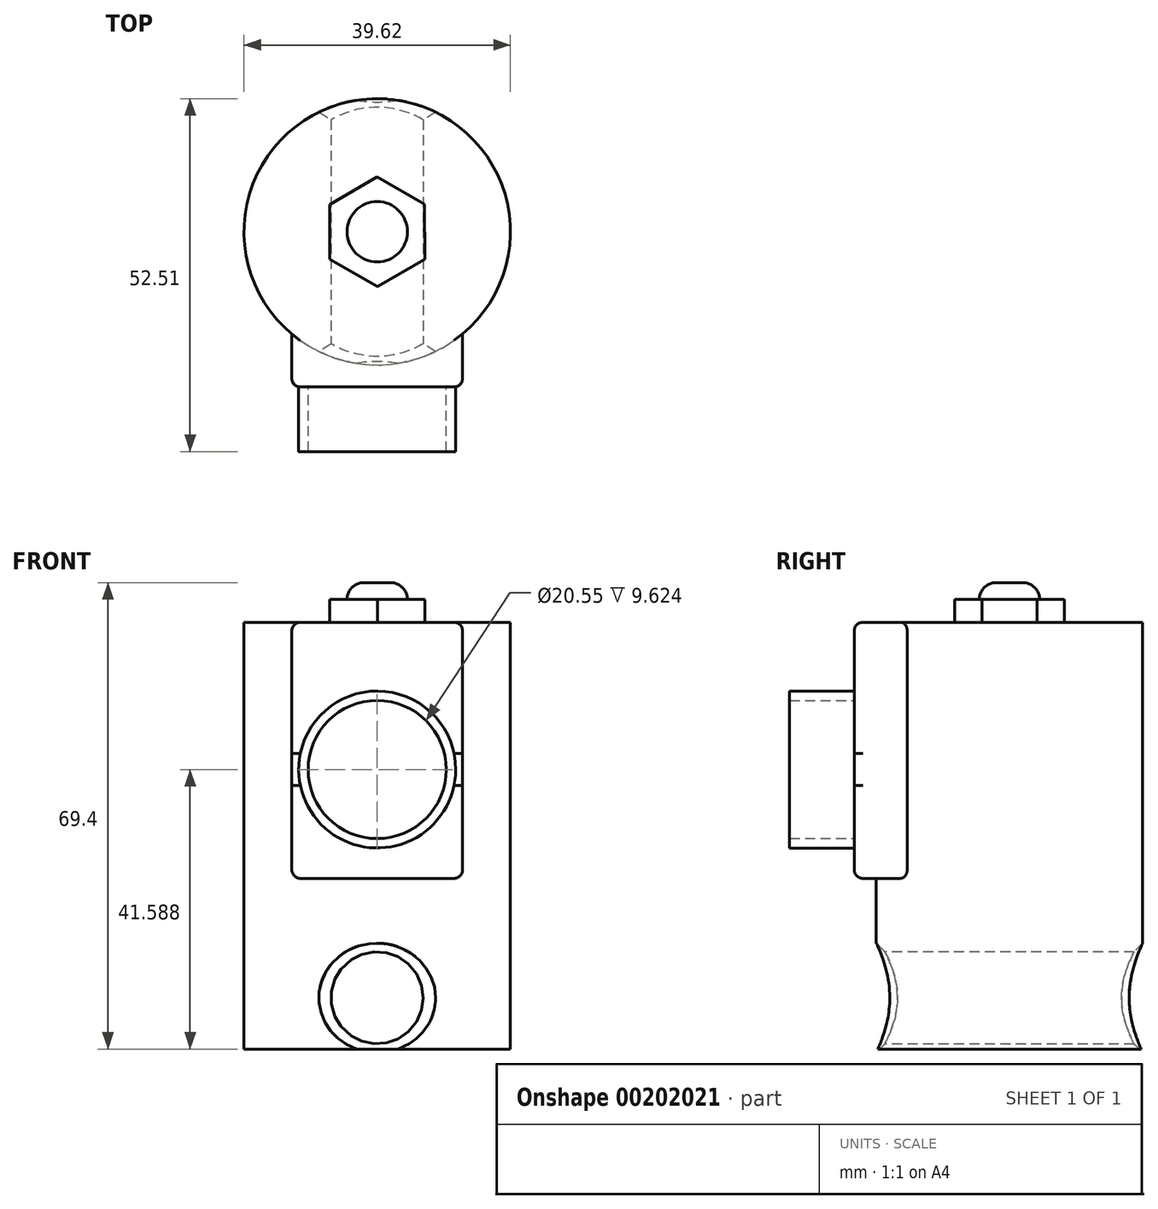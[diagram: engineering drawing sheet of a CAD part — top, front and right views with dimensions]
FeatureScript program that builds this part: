
annotation { "Feature Type Name" : "Feature", "Feature Type Description" : "" }
export const myFeature = defineFeature(function(context is Context, id is Id, definition is map)
    precondition{}
    {
        {
            var Q0;
            Q0=qCreatedBy(makeId("Top.planeOp"),FACE);
            var sketch = newSketch(context, id + "F0", { "sketchPlane" : qUnion([Q0])});
            skCircle(sketch, "E0", {"center": v(0, 0) * mm, "radius": 19.81 * mm});
            skLineSegment(sketch, "E1", {"start": v(0, 0) * mm, "end": v(0, -19.81) * mm});
            skSolve(sketch);
        }
        {
            var Q0;
            Q0=qSketchRegion(id+"F0",true);
            extrude(context, id + "F1", {"entities" : qUnion([Q0]), "depth" : 63.5 * mm});
        }
        {
            var Q0;
            Q0=qCreatedBy(makeId("Right.planeOp"),FACE);
            var sketch = newSketch(context, id + "F2", { "sketchPlane" : qUnion([Q0])});
            skLineSegment(sketch, "E2", {"start": v(-19.81, 0) * mm, "end": v(-19.81, 70.78) * mm});
            skSolve(sketch);
        }
        {
            var Q0;
            Q0=sQuery(id+"F2.wireOp",EDGE,"E2");
            cPlane(context, id + "F3", {"entities" : qUnion([Q0]), "cplaneType" : CPlaneType.LINE_ANGLE, "offset" : 25.4 * mm, "angle" : 90 * degree, "width" : 152.4 * mm, "height" : 152.4 * mm});
        }
        {
            var Q0;
            Q0=qCreatedBy(id+"F3.planeOp",FACE);
            var sketch = newSketch(context, id + "F4", { "sketchPlane" : qUnion([Q0])});
            skLineSegment(sketch, "E3", {"start": v(0, 0) * mm, "end": v(0, 7.62) * mm});
            skCircle(sketch, "E4", {"center": v(0, 7.62) * mm, "radius": 6.86 * mm});
            skSolve(sketch);
        }
        {
            var Q0;
            Q0=makeQuery(id+"F4.imprint","IMPRINT",FACE,{"disambiguationData":[TD([[makeQuery(id+"F4.imprint","IMPRINT",EDGE,{"derivedFrom":sQuery(id+"F4.wireOp",EDGE,"E4")}),1.0]])]});
            extrude(context, id + "F5", {"entities" : qUnion([Q0]), "operationType" : NewBodyOperationType.REMOVE, "depth" : 50.8 * mm});
        }
        {
            var Q0;
            Q0=qCreatedBy(id+"F3.planeOp",FACE);
            var sketch = newSketch(context, id + "F6", { "sketchPlane" : qUnion([Q0])});
            skLineSegment(sketch, "E5", {"start": v(0, 63.5) * mm, "end": v(0, 44.45) * mm});
            skLineSegment(sketch, "E6.bottom", {"start": v(-12.7, 63.5) * mm, "end": v(12.7, 63.5) * mm});
            skLineSegment(sketch, "E6.top", {"start": v(-12.7, 25.4) * mm, "end": v(12.7, 25.4) * mm});
            skLineSegment(sketch, "E6.left", {"start": v(-12.7, 63.5) * mm, "end": v(-12.7, 25.4) * mm});
            skLineSegment(sketch, "E6.right", {"start": v(12.7, 63.5) * mm, "end": v(12.7, 25.4) * mm});
            skPoint(sketch, "E6.middle", {"position": v(0, 44.45) * mm});
            skSolve(sketch);
        }
        {
            var Q0;
            Q0=makeQuery(id+"F6.imprint","IMPRINT",FACE,{"disambiguationData":[TD([[makeQuery(id+"F6.imprint","IMPRINT",EDGE,{"derivedFrom":sQuery(id+"F6.wireOp",EDGE,"E6.top")}),1.0]])]});
            extrude(context, id + "F7", {"entities" : qUnion([Q0]), "operationType" : NewBodyOperationType.ADD, "depth" : 25.4 * mm, "hasSecondDirection" : true, "secondDirectionOppositeDirection" : true, "secondDirectionDepth" : 3.27 * mm});
        }
        {
            var Q0;
            Q0=makeQuery(id+"F7.opExtrude","CAP_FACE",FACE,{"disambiguationData":[OSD([sQuery(id+"F6.wireOp",EDGE,"E6.bottom"),sQuery(id+"F6.wireOp",EDGE,"E6.top"),sQuery(id+"F6.wireOp",EDGE,"E6.left"),sQuery(id+"F6.wireOp",EDGE,"E6.right")])],"isStart":true});
            var sketch = newSketch(context, id + "F8", { "sketchPlane" : qUnion([Q0])});
            skCircle(sketch, "E7", {"center": v(0, 41.59) * mm, "radius": 11.67 * mm});
            skCircle(sketch, "E8", {"center": v(0, 41.59) * mm, "radius": 10.27 * mm});
            skSolve(sketch);
        }
        {
            var Q0;
            Q0=makeQuery(id+"F8.imprint","IMPRINT",FACE,{"disambiguationData":[TD([[makeQuery(id+"F8.imprint","IMPRINT",EDGE,{"derivedFrom":sQuery(id+"F8.wireOp",EDGE,"E7")}),1.0]])]});
            extrude(context, id + "F9", {"entities" : qUnion([Q0]), "operationType" : NewBodyOperationType.ADD, "depth" : 9.62 * mm});
        }
        {
            var Q0;
            Q0=makeQuery(id+"F7.boolean.opBoolean","MERGE",FACE,{"derivedFrom":[makeQuery(id+"F1.opExtrude","CAP_FACE",FACE,{"disambiguationData":[OSD([sQuery(id+"F0.wireOp",EDGE,"E0")])],"isStart":false}),makeQuery(id+"F7.opExtrude","SWEPT_FACE",FACE,{"disambiguationData":[OSD([sQuery(id+"F6.wireOp",EDGE,"E6.bottom")])]})]});
            var sketch = newSketch(context, id + "F10", { "sketchPlane" : qUnion([Q0])});
            skCircle(sketch, "E9.cCircle", {"center": v(0, 0) * mm, "radius": 8.16 * mm, "construction": true});
            skLineSegment(sketch, "E9.0", {"start": v(7.05, 4.1) * mm, "end": v(7.09, -4.06) * mm});
            skLineSegment(sketch, "E9.1", {"start": v(7.09, -4.06) * mm, "end": v(0.03, -8.16) * mm});
            skLineSegment(sketch, "E9.2", {"start": v(0.03, -8.16) * mm, "end": v(-7.05, -4.1) * mm});
            skLineSegment(sketch, "E9.3", {"start": v(-7.05, -4.1) * mm, "end": v(-7.09, 4.06) * mm});
            skLineSegment(sketch, "E9.4", {"start": v(-7.09, 4.06) * mm, "end": v(-0.03, 8.16) * mm});
            skLineSegment(sketch, "E9.5", {"start": v(-0.03, 8.16) * mm, "end": v(7.05, 4.1) * mm});
            skSolve(sketch);
        }
        {
            var Q0;
            Q0=makeQuery(id+"F10.imprint","IMPRINT",FACE,{"disambiguationData":[TD([[makeQuery(id+"F10.imprint","IMPRINT",EDGE,{"derivedFrom":sQuery(id+"F10.wireOp",EDGE,"E9.0")}),-1.0]])]});
            extrude(context, id + "F11", {"entities" : qUnion([Q0]), "operationType" : NewBodyOperationType.ADD, "depth" : 3.38 * mm});
        }
        {
            var Q0;
            Q0=makeQuery(id+"F11.opExtrude","CAP_FACE",FACE,{"disambiguationData":[OSD([sQuery(id+"F10.wireOp",EDGE,"E9.0"),sQuery(id+"F10.wireOp",EDGE,"E9.1"),sQuery(id+"F10.wireOp",EDGE,"E9.2"),sQuery(id+"F10.wireOp",EDGE,"E9.3"),sQuery(id+"F10.wireOp",EDGE,"E9.4"),sQuery(id+"F10.wireOp",EDGE,"E9.5")])],"isStart":false});
            var sketch = newSketch(context, id + "F12", { "sketchPlane" : qUnion([Q0])});
            skCircle(sketch, "E10", {"center": v(0, 0) * mm, "radius": 4.5 * mm});
            skSolve(sketch);
        }
        {
            var Q0;
            Q0=makeQuery(id+"F12.imprint","IMPRINT",FACE,{"disambiguationData":[TD([[makeQuery(id+"F12.imprint","IMPRINT",EDGE,{"derivedFrom":sQuery(id+"F12.wireOp",EDGE,"E10")}),1.0]])]});
            extrude(context, id + "F13", {"entities" : qUnion([Q0]), "operationType" : NewBodyOperationType.ADD, "depth" : 2.53 * mm});
        }
        {
            var Q0;
            Q0=makeQuery(id+"F13.opExtrude","CAP_EDGE",EDGE,{"disambiguationData":[OSD([sQuery(id+"F12.wireOp",EDGE,"E10")])],"isStart":false});
            fillet(context, id + "F14", {"entities" : qUnion([Q0]), "radius" : 2.54 * mm, "tangentPropagation" : true, "allowEdgeOverflow" : false});
        }
        {
            var Q0;
            Q0=makeQuery(id+"F9.opExtrude","CAP_EDGE",EDGE,{"disambiguationData":[OSD([sQuery(id+"F8.wireOp",EDGE,"E7")])],"isStart":true});
            var Q1;
            Q1=makeQuery(id+"F7.opExtrude","CAP_EDGE",EDGE,{"disambiguationData":[OSD([sQuery(id+"F6.wireOp",EDGE,"E6.bottom")])],"isStart":true});
            var Q2;
            Q2=makeQuery(id+"F7.opExtrude","CAP_EDGE",EDGE,{"disambiguationData":[OSD([sQuery(id+"F6.wireOp",EDGE,"E6.top")])],"isStart":true});
            fillet(context, id + "F15", {"entities" : qUnion([Q0, Q1, Q2]), "radius" : 1.27 * mm, "tangentPropagation" : true, "allowEdgeOverflow" : false});
        }
        {
            var Q0;
            Q0=makeQuery(id+"F7.opExtrude","CAP_EDGE",EDGE,{"disambiguationData":[OSD([sQuery(id+"F6.wireOp",EDGE,"E6.left")])],"isStart":true});
            var Q1;
            Q1=makeQuery(id+"F7.opExtrude","CAP_EDGE",EDGE,{"disambiguationData":[OSD([sQuery(id+"F6.wireOp",EDGE,"E6.right")])],"isStart":true});
            fillet(context, id + "F16", {"entities" : qUnion([Q0, Q1]), "radius" : 1.27 * mm, "tangentPropagation" : true, "allowEdgeOverflow" : false});
        }
        {
            var Q0;
            Q0=makeQuery(id+"F5.boolean.opBoolean","INTERSECT",EDGE,{"derivedFrom":[makeQuery(id+"F1.opExtrude","SWEPT_FACE",FACE,{"disambiguationData":[OSD([sQuery(id+"F0.wireOp",EDGE,"E0")])]}),makeQuery(id+"F5.opExtrude","SWEPT_FACE",FACE,{"disambiguationData":[OSD([sQuery(id+"F4.wireOp",EDGE,"E4")])]})]});
            chamfer(context, id + "F17", {"entities" : qUnion([Q0]), "width" : 1.27 * mm, "tangentPropagation" : true});
        }
    });
